# Revit family: DAS107PLUS 1AM  SX
name_source: partatom
category: Porte
revit_build: Autodesk Revit 2018 (Build: 20170223_1515(x64)
units: mm (PartAtom-declared; Revit-internal decimal feet)

## family parameters
Condiviso = No
Host = Muro
Numero OmniClass = 23.30.10.00
Punto di calcolo locali = No
Sempre verticale = Sì
Taglio con vuoti quando caricato = No
Titolo OmniClass = Doors

## types (1)
- DAS107PLUS 1AM  SX
    Altezza = 2000 mm  [stored 6.56168 ft]
    Auxiliary power = 0.64 A @ 24 Vdc
    BIMobject Category = Sliding
    Brand = Ditec
    Brand url = http://www.ditecentrematic.com
    Calc Width = 1500 mm  [stored 4.92126 ft]
    Chiusura muro = Per host
    Description = automation for sliding doors
    Design country = Italy
    Dimensions (H x D x L) = 120x140xL mm
    Drive type = electromechanical unit
    Edition number = 1
    Frame = Aluminum + Glass
    Gearmotor = 24V Vdc with encoder
    IFC Classification = Door
    Larghezza = 1500 mm  [stored 4.92126 ft]
    Manufacturer country = China
    Manufacturer name = Entrematic Italy
    Masterformat 2016 Code = 08 01 32
    Masterformat 2016 Description = Operation and Maintenance of Sliding Glass Doors
    Max Operator Length = 5600 mm  [stored 18.3727 ft]
    Max nominal power = 75 W
    NBS Reference Code = 25-30-20-77
    NBS Reference Description = Sliding Doorset Systems
    OmniClass Code = 23-17 11 00
    OmniClass Description = Doors
    Operating temperature = -20 ° C / +50 ° C
    Operator = Aluminum
    Operator Length = 3400 mm  [stored 11.1549 ft]
    Power supply = 100÷240 Vac @ 50/60 MHz
    Product family = Automatic Doors
    Product group = Sliding Automatic Doors
    Protection rating = IP20
    UNSPSC Code = 301715
    Unicalss 2015 Code = Pr 73_30_23_05
    Uniclass 1.4 Code = JL20
    Uniclass 1.4 Description = Doors
    Uniclass 2.0 Code = SS_25-30-20-77
    Uniclass 2.0 Description = Sliding Doorset Systems
    Uniclass 2015 Name = Automatic sliding door operator
    Weight = 0.00 kN

note: [stored X ft] marks values corroborated as IEEE doubles in the binary element streams (Revit-internal decimal feet)

## geometry (parser evidence)
native form markers: Sweep x1
no freeform markers — native parametric forms only
